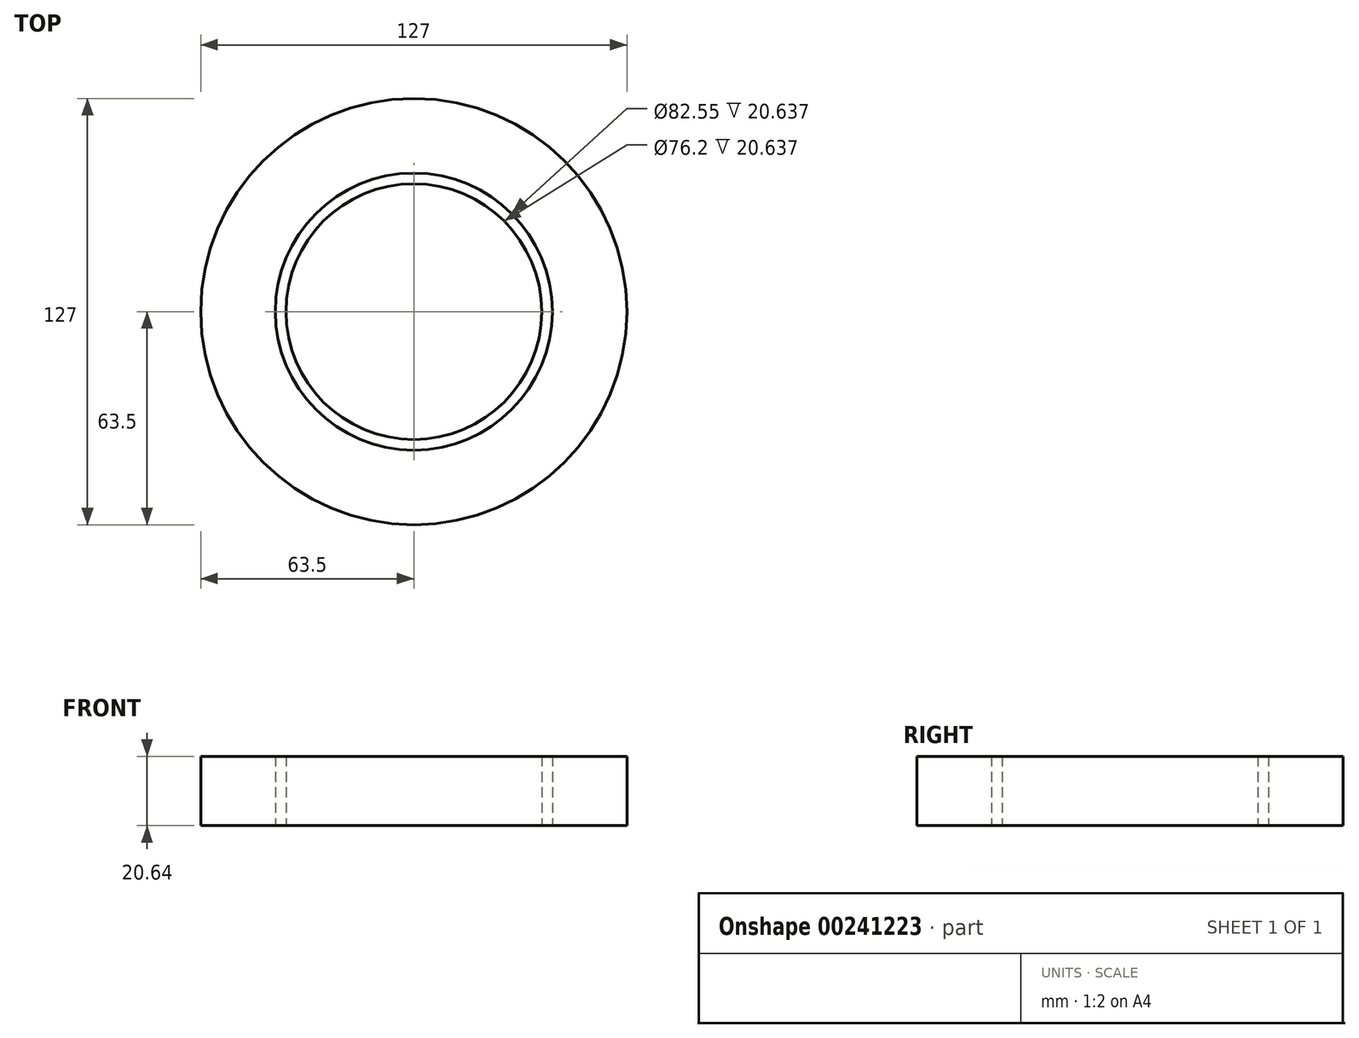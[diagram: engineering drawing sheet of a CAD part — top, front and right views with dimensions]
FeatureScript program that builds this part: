
annotation { "Feature Type Name" : "Feature", "Feature Type Description" : "" }
export const myFeature = defineFeature(function(context is Context, id is Id, definition is map)
    precondition{}
    {
        {
            var Q0;
            Q0=qCreatedBy(makeId("Top.planeOp"),FACE);
            var sketch = newSketch(context, id + "F0", { "sketchPlane" : qUnion([Q0])});
            skCircle(sketch, "E0", {"center": v(0, 0) * mm, "radius": 38.1 * mm});
            skCircle(sketch, "E1", {"center": v(0, 0) * mm, "radius": 41.28 * mm});
            skSolve(sketch);
        }
        {
            var Q0;
            Q0=makeQuery(id+"F0.imprint","IMPRINT",FACE,{"disambiguationData":[TD([[makeQuery(id+"F0.imprint","IMPRINT",EDGE,{"derivedFrom":sQuery(id+"F0.wireOp",EDGE,"E0")}),-1.0]])]});
            extrude(context, id + "F1", {"entities" : qUnion([Q0]), "depth" : 20.64 * mm});
        }
        {
            var Q0;
            Q0=qCreatedBy(makeId("Top.planeOp"),FACE);
            var sketch = newSketch(context, id + "F2", { "sketchPlane" : qUnion([Q0])});
            skCircle(sketch, "E2.0", {"center": v(0, 0) * mm, "radius": 41.28 * mm});
            skSolve(sketch);
        }
        {
            var Q0;
            Q0=qCreatedBy(makeId("Top.planeOp"),FACE);
            var sketch = newSketch(context, id + "F3", { "sketchPlane" : qUnion([Q0])});
            skCircle(sketch, "E3.0", {"center": v(0, 0) * mm, "radius": 41.28 * mm});
            skCircle(sketch, "E4.0", {"center": v(0, 0) * mm, "radius": 63.5 * mm});
            skSolve(sketch);
        }
        {
            var Q0;
            Q0 = qSketchRegion(id + "F3", true);
            extrude(context, id + "F4", {"entities" : qUnion([Q0]), "depth" : 20.64 * mm});
        }
    });
